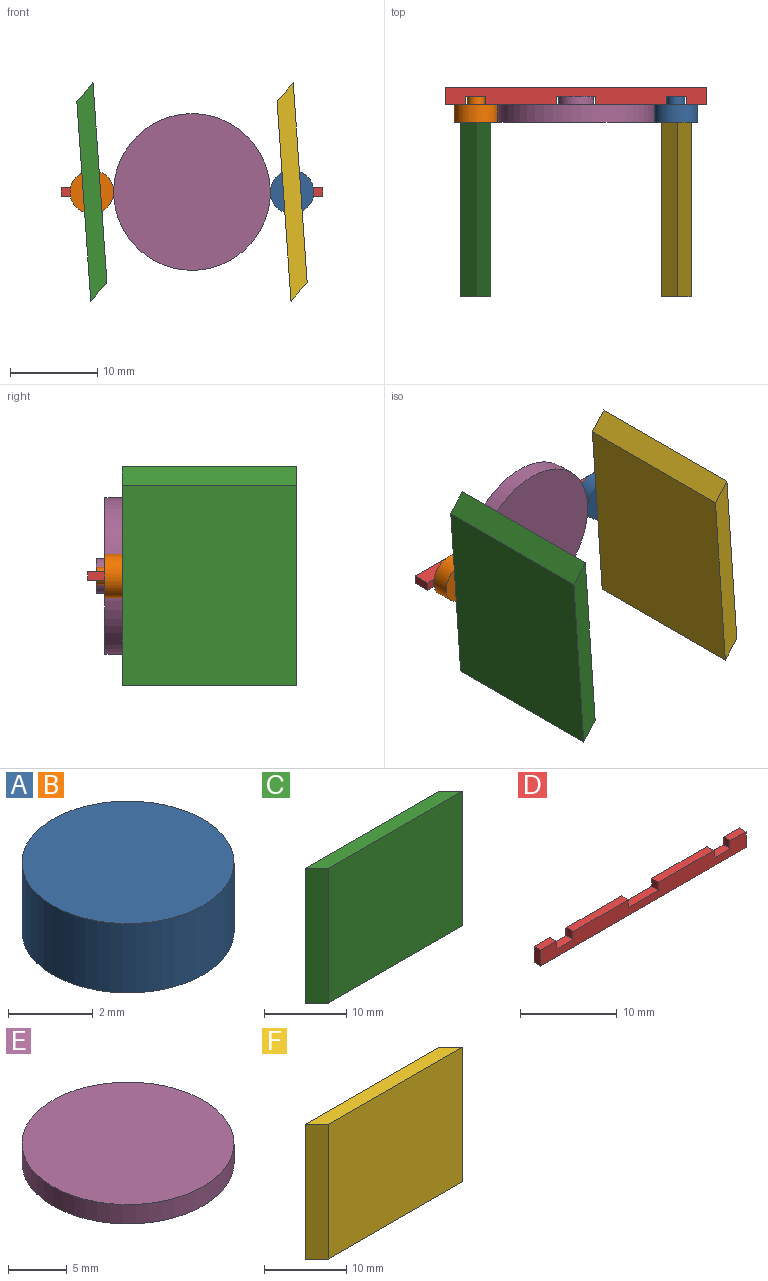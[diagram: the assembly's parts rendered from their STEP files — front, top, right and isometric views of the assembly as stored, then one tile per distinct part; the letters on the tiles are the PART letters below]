
ASSEMBLY  parts=6 mates=5
PART A: 13 faces, bbox 5x5x3 mm
  f0: plane 1x0.63mm, normal (0,0,-1), area 0.5mm2, adj f4,f5,f9,f11
  f1: plane 5x5mm, normal (0,0,-1), area 15.4mm2, adj f2,f4,f5,f6,f7,f8,f9,f11
  f2: cylinder r=2.5mm len=5mm, axis (0,0,1), area 31.4mm2, adj f1,f3
  f3: plane 5x5mm, normal (0,0,1), area 19.6mm2, adj f2
  f4: plane 1x1mm, normal (0,-1,0), area 1mm2, adj f0,f1,f5,f9
  f5: plane 1x0.63mm, normal (-1,0,0), area 0.6mm2, adj f0,f1,f4,f11
  f6: plane 1x0.63mm, normal (-1,0,0), area 0.6mm2, adj f1,f7,f10,f11
  f7: plane 1x1mm, normal (0,1,0), area 1mm2, adj f1,f6,f8,f10
  f8: plane 1x0.63mm, normal (1,0,0), area 0.6mm2, adj f1,f7,f10,f11
  f9: plane 1x0.63mm, normal (1,0,0), area 0.6mm2, adj f0,f1,f4,f11
  f10: plane 1x0.63mm, normal (0,0,-1), area 0.5mm2, adj f6,f7,f8,f11
  f11: cylinder r=1mm len=2mm, axis (0,0,1), area 8.4mm2, adj f0,f1,f5,f6,f8,f9,f10,f12
  f12: plane 2x2mm, normal (0,0,-1), area 3.1mm2, adj f11
PART B: same geometry as A
PART C: 6 faces, bbox 25x2x20 mm
  f0: plane 23x20mm, normal (0,-1,0), area 460mm2, adj f1,f3,f4,f5
  f1: plane 20x2mm, normal (0.71,0.71,0), area 56.6mm2, adj f0,f2,f4,f5
  f2: plane 23x20mm, normal (0,1,0), area 460mm2, adj f1,f3,f4,f5
  f3: plane 20x2mm, normal (-0.71,-0.71,0), area 56.6mm2, adj f0,f2,f4,f5
  f4: plane 25x2mm, normal (0,0,1), area 46mm2, adj f0,f1,f2,f3
  f5: plane 25x2mm, normal (0,0,-1), area 46mm2, adj f0,f1,f2,f3
PART D: 18 faces, bbox 30x1x2 mm
  f0: plane 30x2mm, normal (0,1,0), area 51mm2, adj f1,f3,f4,f5,f6,f7,f8,f9
  f1: cylinder r=1.25mm len=1mm, axis (0,0,1), area 1mm2, adj f0,f2,f4,f5
  f2: plane 30x2mm, normal (0,-1,0), area 51mm2, adj f1,f3,f4,f5,f6,f7,f8,f9
  f3: cylinder r=2.25mm len=1mm, axis (0,0,1), area 1mm2, adj f0,f2,f4,f6
  f4: plane 8.16x1mm, normal (0,0,1), area 8.1mm2, adj f0,f1,f2,f3
  f5: plane 2.5x1mm, normal (0,0,1), area 2.4mm2, adj f0,f1,f2,f12
  f6: plane 4.5x1mm, normal (0,0,1), area 4.5mm2, adj f0,f2,f3,f7
  f7: cylinder r=2.25mm len=1mm, axis (0,0,1), area 1mm2, adj f0,f2,f6,f9
  f8: cylinder r=1.25mm len=1mm, axis (0,0,1), area 1mm2, adj f0,f2,f9,f10
  f9: plane 8.16x1mm, normal (0,0,1), area 8.1mm2, adj f0,f2,f7,f8
  f10: plane 2.5x1mm, normal (0,0,1), area 2.4mm2, adj f0,f2,f8,f14
  f11: plane 2x1mm, normal (1,0,0), area 2mm2, adj f0,f2,f13,f17
  f12: cylinder r=1.25mm len=1mm, axis (0,0,1), area 1mm2, adj f0,f2,f5,f13
  f13: plane 2.35x1mm, normal (0,0,1), area 2.3mm2, adj f0,f2,f11,f12
  f14: cylinder r=1.25mm len=1mm, axis (0,0,1), area 1mm2, adj f0,f2,f10,f16
  f15: plane 2x1mm, normal (-1,0,0), area 2mm2, adj f0,f2,f16,f17
  f16: plane 2.35x1mm, normal (0,0,1), area 2.3mm2, adj f0,f2,f14,f15
  f17: plane 30x1mm, normal (0,0,-1), area 30mm2, adj f0,f2,f11,f15
PART E: 13 faces, bbox 18x18x3 mm
  f0: plane 5.77x2mm, normal (0,0,-1), area 11.2mm2, adj f4,f5,f6,f11
  f1: plane 18x18mm, normal (0,0,-1), area 219.6mm2, adj f2,f4,f5,f6,f7,f8,f9,f11
  f2: cylinder r=9mm len=18mm, axis (0,0,1), area 113.1mm2, adj f1,f3
  f3: plane 18x18mm, normal (0,0,1), area 254.5mm2, adj f2
  f4: plane 5.77x1mm, normal (1,0,0), area 5.8mm2, adj f0,f1,f5,f11
  f5: plane 2x1mm, normal (0,-1,0), area 2mm2, adj f0,f1,f4,f6
  f6: plane 5.77x1mm, normal (-1,0,0), area 5.8mm2, adj f0,f1,f5,f11
  f7: plane 5.77x1mm, normal (-1,0,0), area 5.8mm2, adj f1,f8,f10,f11
  f8: plane 2x1mm, normal (0,1,0), area 2mm2, adj f1,f7,f9,f10
  f9: plane 5.77x1mm, normal (1,0,0), area 5.8mm2, adj f1,f8,f10,f11
  f10: plane 5.77x2mm, normal (0,0,-1), area 11.2mm2, adj f7,f8,f9,f11
  f11: cylinder r=2mm len=4mm, axis (0,0,1), area 16.8mm2, adj f0,f1,f4,f6,f7,f9,f10,f12
  f12: plane 4x4mm, normal (0,0,-1), area 12.6mm2, adj f11
PART F: 6 faces, bbox 25x2x20 mm
  f0: plane 23x20mm, normal (0,-1,0), area 460mm2, adj f1,f3,f4,f5
  f1: plane 20x2mm, normal (0.71,0.71,0), area 56.6mm2, adj f0,f2,f4,f5
  f2: plane 23x20mm, normal (0,1,0), area 460mm2, adj f1,f3,f4,f5
  f3: plane 20x2mm, normal (-0.71,-0.71,0), area 56.6mm2, adj f0,f2,f4,f5
  f4: plane 25x2mm, normal (0,0,1), area 46mm2, adj f0,f1,f2,f3
  f5: plane 25x2mm, normal (0,0,-1), area 46mm2, adj f0,f1,f2,f3
PLACE A rot(axis=(0.55,-0.59,0.59),122.3deg) t=(11.63,-4,12.54)mm
PLACE B rot(axis=(0.55,-0.59,0.59),122.3deg) t=(-11.37,-4,12.54)mm
PLACE C rot(axis=(0.55,-0.59,0.59),122.3deg) t=(-11.37,-4,12.54)mm
PLACE D rot(axis=(0,-0.71,0.71),180deg) t=(-1,-4,1)mm
PLACE E rot(axis=(0.55,0.59,-0.59),122.3deg) t=(-1.07,-4,-0.93)mm
PLACE F rot(axis=(0.55,-0.59,0.59),122.3deg) t=(13.23,-4,-10.4)mm
MATE fastened B.f2 <-> C.f5  axis (0,-1,0) through (-11.5,-4,0)mm
MATE fastened F.f5 <-> A.f2  axis (0,1,0) through (11.5,-4,0)mm
MATE revolute E.f2 <-> D.f3  axis (0,1,0) through (0,-1,0)mm
MATE revolute A.f2 <-> D.f8  axis (0,1,0) through (11.5,-1,0)mm
MATE revolute B.f2 <-> D.f1  axis (0,1,0) through (-11.5,-1,0)mm
